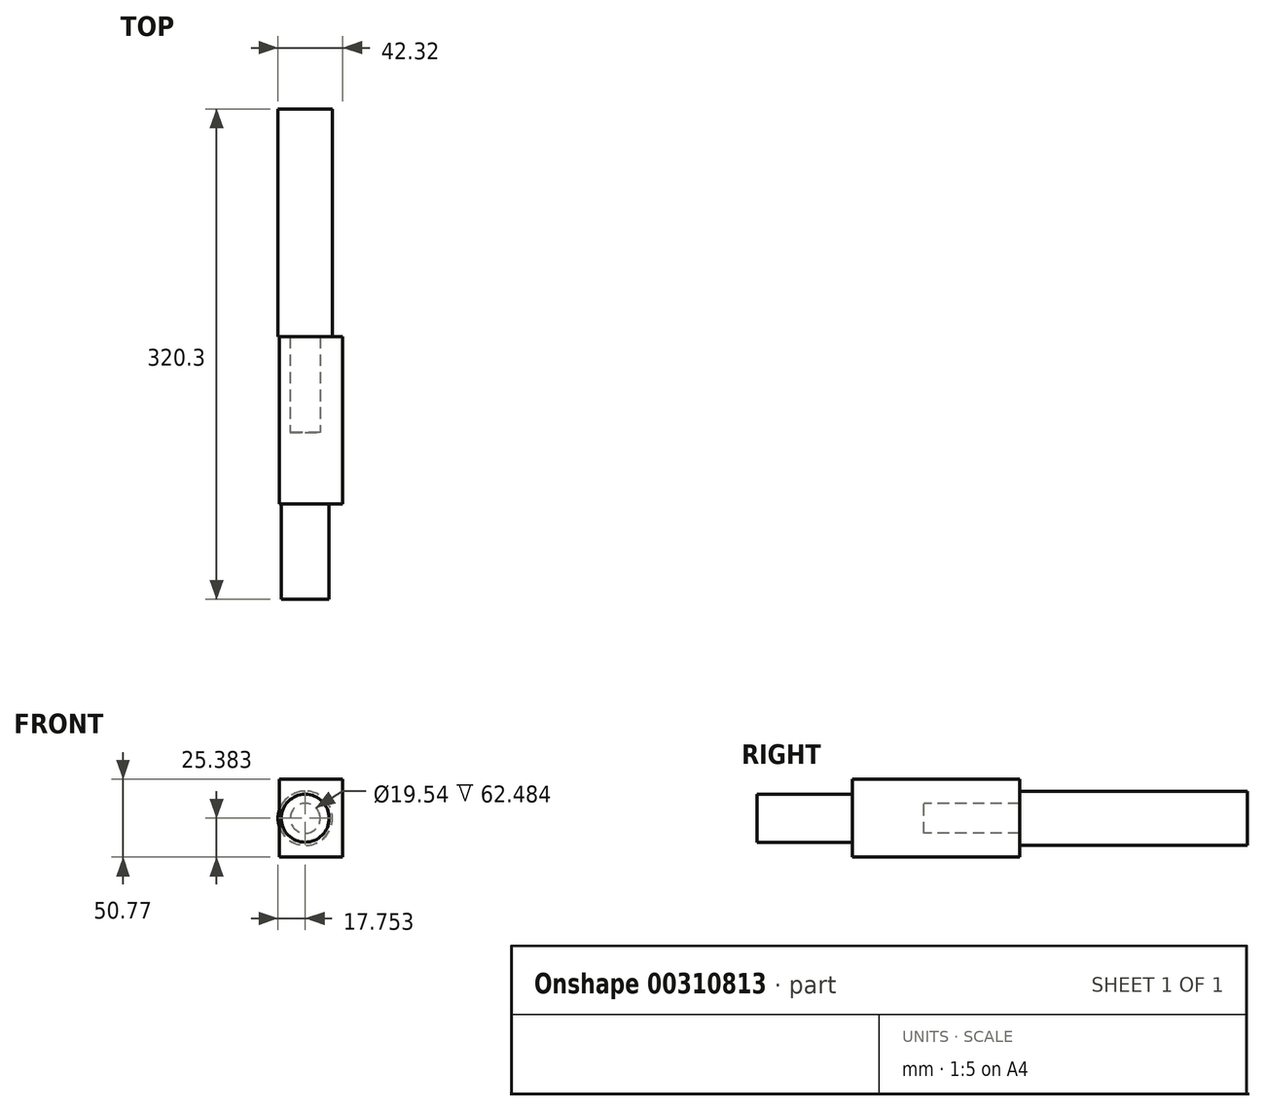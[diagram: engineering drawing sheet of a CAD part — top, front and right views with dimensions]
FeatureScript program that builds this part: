
annotation { "Feature Type Name" : "Feature", "Feature Type Description" : "" }
export const myFeature = defineFeature(function(context is Context, id is Id, definition is map)
    precondition{}
    {
        {
            var Q0;
            Q0=qCreatedBy(makeId("Front.planeOp"),FACE);
            var sketch = newSketch(context, id + "F0", { "sketchPlane" : qUnion([Q0])});
            skLineSegment(sketch, "E0.bottom", {"start": v(-108.3, 0) * mm, "end": v(-66.8, 0) * mm});
            skLineSegment(sketch, "E0.top", {"start": v(-108.3, -50.77) * mm, "end": v(-66.8, -50.77) * mm});
            skLineSegment(sketch, "E0.left", {"start": v(-108.3, 0) * mm, "end": v(-108.3, -50.77) * mm});
            skLineSegment(sketch, "E0.right", {"start": v(-66.8, 0) * mm, "end": v(-66.8, -50.77) * mm});
            skCircle(sketch, "E1", {"center": v(-91.38, -25.39) * mm, "radius": 9.77 * mm});
            skPoint(sketch, "E1.centerSnap0", {"position": v(-108.3, -25.39) * mm});
            skSolve(sketch);
        }
        {
            var Q0;
            Q0 = qSketchRegion(id + "F0", true);
            extrude(context, id + "F1", {"entities" : qUnion([Q0]), "oppositeDirection" : true, "depth" : 62.48 * mm});
        }
        {
            var Q0;
            Q0=makeQuery(id+"F1.opExtrude","CAP_FACE",FACE,{"disambiguationData":[OSD([sQuery(id+"F0.wireOp",EDGE,"E0.bottom"),sQuery(id+"F0.wireOp",EDGE,"E0.top"),sQuery(id+"F0.wireOp",EDGE,"E0.left"),sQuery(id+"F0.wireOp",EDGE,"E0.right"),sQuery(id+"F0.wireOp",EDGE,"E1")])],"isStart":true});
            var sketch = newSketch(context, id + "F2", { "sketchPlane" : qUnion([Q0])});
            skCircle(sketch, "E2", {"center": v(-91.38, -25.39) * mm, "radius": 15.64 * mm});
            skSolve(sketch);
        }
        {
            var Q0;
            Q0 = qSketchRegion(id + "F2", true);
            var Q1;
            Q1=makeQuery(id+"F1.opExtrude","CAP_FACE",FACE,{"disambiguationData":[OSD([sQuery(id+"F0.wireOp",EDGE,"E0.bottom"),sQuery(id+"F0.wireOp",EDGE,"E0.top"),sQuery(id+"F0.wireOp",EDGE,"E0.left"),sQuery(id+"F0.wireOp",EDGE,"E0.right"),sQuery(id+"F0.wireOp",EDGE,"E1")])],"isStart":false});
            extrude(context, id + "F3", {"entities" : qUnion([Q0, Q1]), "operationType" : NewBodyOperationType.ADD, "depth" : 108.97 * mm});
        }
        {
            var Q0;
            Q0=makeQuery(id+"F1.opExtrude","CAP_FACE",FACE,{"disambiguationData":[OSD([sQuery(id+"F0.wireOp",EDGE,"E0.bottom"),sQuery(id+"F0.wireOp",EDGE,"E0.top"),sQuery(id+"F0.wireOp",EDGE,"E0.left"),sQuery(id+"F0.wireOp",EDGE,"E0.right"),sQuery(id+"F0.wireOp",EDGE,"E1")])],"isStart":false});
            var sketch = newSketch(context, id + "F4", { "sketchPlane" : qUnion([Q0])});
            skCircle(sketch, "E3", {"center": v(91.38, -25.39) * mm, "radius": 17.75 * mm});
            skSolve(sketch);
        }
        {
            var Q0;
            Q0 = qSketchRegion(id + "F4", true);
            extrude(context, id + "F5", {"entities" : qUnion([Q0]), "operationType" : NewBodyOperationType.ADD, "depth" : 148.84 * mm});
        }
    });
